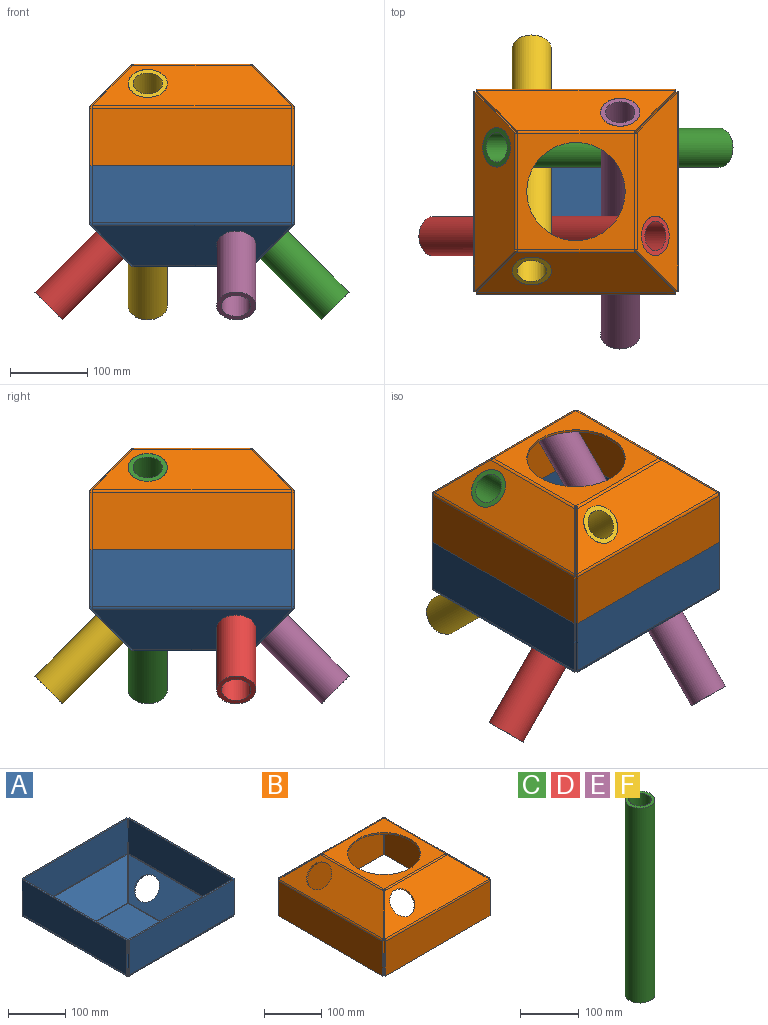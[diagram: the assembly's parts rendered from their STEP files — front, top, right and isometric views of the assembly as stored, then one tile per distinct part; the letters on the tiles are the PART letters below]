
ASSEMBLY  parts=6 mates=5
PART A: 82 faces, bbox 264.7x264.7x131 mm
  f0: plane 150.51x150.51mm, normal (0,0,-1), area 22652.1mm2, adj f20,f40,f60,f80
  f1: plane 150.51x150.51mm, normal (0,0,1), area 22652.1mm2, adj f21,f41,f61,f81
  f2: plane 2.25x2.25mm, normal (0,-0.71,-0.71), area 5.1mm2, adj f3,f7,f8,f18
  f3: plane 53.86x53.86mm, normal (0.82,-0.41,-0.41), area 283.8mm2, adj f2,f7,f8,f15
  f4: plane 2.25x2.25mm, normal (0,-0.71,-0.71), area 5.1mm2, adj f6,f7,f8,f19
  f5: cylinder r=25.4mm len=50.8mm, axis (0,0.71,-0.71), area 506.7mm2, adj f7,f8
  f6: plane 53.86x53.86mm, normal (-0.82,-0.41,-0.41), area 283.8mm2, adj f4,f7,f8,f14
  f7: plane 256.92x51.61mm, normal (0,0.71,-0.71), area 12959mm2, adj f2,f3,f4,f5,f6,f16,f20
  f8: plane 256.92x51.61mm, normal (0,-0.71,0.71), area 12959mm2, adj f2,f3,f4,f5,f6,f17,f21
  f9: plane 258.25x3.18mm, normal (0,0,1), area 820mm2, adj f10,f11,f12,f13
  f10: plane 73.94x3.18mm, normal (1,0,0), area 234.8mm2, adj f9,f12,f13,f15
  f11: plane 73.94x3.18mm, normal (-1,0,0), area 234.8mm2, adj f9,f12,f13,f14
  f12: plane 258.25x73.94mm, normal (0,1,0), area 19094.7mm2, adj f9,f10,f11,f16
  f13: plane 258.25x73.94mm, normal (0,-1,0), area 19094.7mm2, adj f9,f10,f11,f17
  f14: bspline ~3.86x3.84mm, area 10mm2, adj f6,f11,f16,f17
  f15: bspline ~3.86x3.84mm, area 10mm2, adj f3,f10,f16,f17
  f16: cylinder r=5.46mm len=258.25mm, axis (-1,0,0), area 1104.8mm2, adj f7,f12,f14,f15
  f17: cylinder r=2.29mm len=258.25mm, axis (-1,0,0), area 462.5mm2, adj f8,f13,f14,f15
  f18: plane 3.86x3.84mm, normal (1,0,0), area 9.7mm2, adj f2,f20,f21,f79
  f19: plane 3.86x3.84mm, normal (-1,0,0), area 9.7mm2, adj f4,f20,f21,f59
  f20: cylinder r=5.46mm len=150.51mm, axis (1,0,0), area 645.5mm2, adj f0,f7,f18,f19
  f21: cylinder r=2.29mm len=150.51mm, axis (1,0,0), area 270.2mm2, adj f1,f8,f18,f19
  f22: plane 2.25x2.25mm, normal (0,0.71,-0.71), area 5.1mm2, adj f23,f27,f28,f39
  f23: plane 53.86x53.86mm, normal (-0.82,0.41,-0.41), area 283.8mm2, adj f22,f27,f28,f35
  f24: plane 2.25x2.25mm, normal (0,0.71,-0.71), area 5.1mm2, adj f26,f27,f28,f38
  f25: cylinder r=25.4mm len=50.8mm, axis (0,-0.71,-0.71), area 506.7mm2, adj f27,f28
  f26: plane 53.86x53.86mm, normal (0.82,0.41,-0.41), area 283.8mm2, adj f24,f27,f28,f34
  f27: plane 256.92x51.61mm, normal (0,-0.71,-0.71), area 12959mm2, adj f22,f23,f24,f25,f26,f36,f40
  f28: plane 256.92x51.61mm, normal (0,0.71,0.71), area 12959mm2, adj f22,f23,f24,f25,f26,f37,f41
  f29: plane 258.25x3.18mm, normal (0,0,1), area 820mm2, adj f30,f31,f32,f33
  f30: plane 73.94x3.18mm, normal (-1,0,0), area 234.8mm2, adj f29,f32,f33,f35
  f31: plane 73.94x3.18mm, normal (1,0,0), area 234.8mm2, adj f29,f32,f33,f34
  f32: plane 258.25x73.94mm, normal (0,-1,0), area 19094.7mm2, adj f29,f30,f31,f36
  f33: plane 258.25x73.94mm, normal (0,1,0), area 19094.7mm2, adj f29,f30,f31,f37
  f34: bspline ~3.86x3.84mm, area 10mm2, adj f26,f31,f36,f37
  f35: bspline ~3.86x3.84mm, area 10mm2, adj f23,f30,f36,f37
  f36: cylinder r=5.46mm len=258.25mm, axis (1,0,0), area 1104.8mm2, adj f27,f32,f34,f35
  f37: cylinder r=2.29mm len=258.25mm, axis (1,0,0), area 462.5mm2, adj f28,f33,f34,f35
  f38: plane 3.86x3.84mm, normal (1,0,0), area 9.7mm2, adj f24,f40,f41,f78
  f39: plane 3.86x3.84mm, normal (-1,0,0), area 9.7mm2, adj f22,f40,f41,f58
  f40: cylinder r=5.46mm len=150.51mm, axis (1,0,0), area 645.5mm2, adj f0,f27,f38,f39
  f41: cylinder r=2.29mm len=150.51mm, axis (1,0,0), area 270.2mm2, adj f1,f28,f38,f39
  f42: plane 2.25x2.25mm, normal (0.71,0,-0.71), area 5.1mm2, adj f43,f47,f48,f59
  f43: plane 53.86x53.86mm, normal (0.41,0.82,-0.41), area 283.8mm2, adj f42,f47,f48,f55
  f44: plane 2.25x2.25mm, normal (0.71,0,-0.71), area 5.1mm2, adj f46,f47,f48,f58
  f45: cylinder r=25.4mm len=50.8mm, axis (-0.71,0,-0.71), area 506.7mm2, adj f47,f48
  f46: plane 53.86x53.86mm, normal (0.41,-0.82,-0.41), area 283.8mm2, adj f44,f47,f48,f54
  f47: plane 256.92x51.61mm, normal (-0.71,0,-0.71), area 12959mm2, adj f42,f43,f44,f45,f46,f56,f60
  f48: plane 256.92x51.61mm, normal (0.71,0,0.71), area 12959mm2, adj f42,f43,f44,f45,f46,f57,f61
  f49: plane 258.25x3.18mm, normal (0,0,1), area 820mm2, adj f50,f51,f52,f53
  f50: plane 73.94x3.18mm, normal (0,1,0), area 234.8mm2, adj f49,f52,f53,f55
  f51: plane 73.94x3.18mm, normal (0,-1,0), area 234.8mm2, adj f49,f52,f53,f54
  f52: plane 258.25x73.94mm, normal (-1,0,0), area 19094.7mm2, adj f49,f50,f51,f56
  f53: plane 258.25x73.94mm, normal (1,0,0), area 19094.7mm2, adj f49,f50,f51,f57
  f54: bspline ~3.86x3.84mm, area 10mm2, adj f46,f51,f56,f57
  f55: bspline ~3.86x3.84mm, area 10mm2, adj f43,f50,f56,f57
  f56: cylinder r=5.46mm len=258.25mm, axis (0,-1,0), area 1104.8mm2, adj f47,f52,f54,f55
  f57: cylinder r=2.29mm len=258.25mm, axis (0,-1,0), area 462.5mm2, adj f48,f53,f54,f55
  f58: plane 3.86x3.84mm, normal (0,-1,0), area 9.7mm2, adj f39,f44,f60,f61
  f59: plane 3.86x3.84mm, normal (0,1,0), area 9.7mm2, adj f19,f42,f60,f61
  f60: cylinder r=5.46mm len=150.51mm, axis (0,-1,0), area 645.5mm2, adj f0,f47,f58,f59
  f61: cylinder r=2.29mm len=150.51mm, axis (0,-1,0), area 270.2mm2, adj f1,f48,f58,f59
  f62: plane 2.25x2.25mm, normal (-0.71,0,-0.71), area 5.1mm2, adj f63,f67,f68,f78
  f63: plane 53.86x53.86mm, normal (-0.41,-0.82,-0.41), area 283.8mm2, adj f62,f67,f68,f75
  f64: plane 2.25x2.25mm, normal (-0.71,0,-0.71), area 5.1mm2, adj f66,f67,f68,f79
  f65: cylinder r=25.4mm len=50.8mm, axis (0.71,0,-0.71), area 506.7mm2, adj f67,f68
  f66: plane 53.86x53.86mm, normal (-0.41,0.82,-0.41), area 283.8mm2, adj f64,f67,f68,f74
  f67: plane 256.92x51.61mm, normal (0.71,0,-0.71), area 12959mm2, adj f62,f63,f64,f65,f66,f76,f80
  f68: plane 256.92x51.61mm, normal (-0.71,0,0.71), area 12959mm2, adj f62,f63,f64,f65,f66,f77,f81
  f69: plane 258.25x3.18mm, normal (0,0,1), area 820mm2, adj f70,f71,f72,f73
  f70: plane 73.94x3.18mm, normal (0,-1,0), area 234.8mm2, adj f69,f72,f73,f75
  f71: plane 73.94x3.18mm, normal (0,1,0), area 234.8mm2, adj f69,f72,f73,f74
  f72: plane 258.25x73.94mm, normal (1,0,0), area 19094.7mm2, adj f69,f70,f71,f76
  f73: plane 258.25x73.94mm, normal (-1,0,0), area 19094.7mm2, adj f69,f70,f71,f77
  f74: bspline ~3.86x3.84mm, area 10mm2, adj f66,f71,f76,f77
  f75: bspline ~3.86x3.84mm, area 10mm2, adj f63,f70,f76,f77
  f76: cylinder r=5.46mm len=258.25mm, axis (0,1,0), area 1104.8mm2, adj f67,f72,f74,f75
  f77: cylinder r=2.29mm len=258.25mm, axis (0,1,0), area 462.5mm2, adj f68,f73,f74,f75
  f78: plane 3.86x3.84mm, normal (0,-1,0), area 9.7mm2, adj f38,f62,f80,f81
  f79: plane 3.86x3.84mm, normal (0,1,0), area 9.7mm2, adj f18,f64,f80,f81
  f80: cylinder r=5.46mm len=150.51mm, axis (0,-1,0), area 645.5mm2, adj f0,f67,f78,f79
  f81: cylinder r=2.29mm len=150.51mm, axis (0,-1,0), area 270.2mm2, adj f1,f68,f78,f79
PART B: 83 faces, bbox 264.7x264.7x131 mm
  f0: cylinder r=63.5mm len=127mm, axis (0,0,1), area 1266.8mm2, adj f1,f2
  f1: plane 150.51x150.51mm, normal (0,0,-1), area 9984.4mm2, adj f0,f22,f42,f62,f82
  f2: plane 150.51x150.51mm, normal (0,0,1), area 9984.4mm2, adj f0,f21,f41,f61,f81
  f3: plane 2.25x2.25mm, normal (0,0.71,0.71), area 5.1mm2, adj f7,f8,f9,f19
  f4: plane 53.86x53.86mm, normal (-0.82,0.41,0.41), area 283.8mm2, adj f5,f8,f9,f15
  f5: plane 2.25x2.25mm, normal (0,0.71,0.71), area 5.1mm2, adj f4,f8,f9,f20
  f6: cylinder r=25.4mm len=50.8mm, axis (0,0.71,-0.71), area 506.7mm2, adj f8,f9
  f7: plane 53.86x53.86mm, normal (0.82,0.41,0.41), area 283.8mm2, adj f3,f8,f9,f16
  f8: plane 256.92x51.61mm, normal (0,0.71,-0.71), area 12959mm2, adj f3,f4,f5,f6,f7,f18,f22
  f9: plane 256.92x51.61mm, normal (0,-0.71,0.71), area 12959mm2, adj f3,f4,f5,f6,f7,f17,f21
  f10: plane 258.25x3.18mm, normal (0,0,-1), area 820mm2, adj f11,f12,f13,f14
  f11: plane 73.94x3.18mm, normal (-1,0,0), area 234.8mm2, adj f10,f13,f14,f15
  f12: plane 73.94x3.18mm, normal (1,0,0), area 234.8mm2, adj f10,f13,f14,f16
  f13: plane 258.25x73.94mm, normal (0,1,0), area 19094.7mm2, adj f10,f11,f12,f18
  f14: plane 258.25x73.94mm, normal (0,-1,0), area 19094.7mm2, adj f10,f11,f12,f17
  f15: bspline ~3.86x3.84mm, area 10mm2, adj f4,f11,f17,f18
  f16: bspline ~3.86x3.84mm, area 10mm2, adj f7,f12,f17,f18
  f17: cylinder r=5.46mm len=258.25mm, axis (-1,0,0), area 1104.8mm2, adj f9,f14,f15,f16
  f18: cylinder r=2.29mm len=258.25mm, axis (-1,0,0), area 462.5mm2, adj f8,f13,f15,f16
  f19: plane 3.86x3.84mm, normal (1,0,0), area 9.7mm2, adj f3,f21,f22,f80
  f20: plane 3.86x3.84mm, normal (-1,0,0), area 9.7mm2, adj f5,f21,f22,f59
  f21: cylinder r=5.46mm len=150.51mm, axis (1,0,0), area 645.5mm2, adj f2,f9,f19,f20
  f22: cylinder r=2.29mm len=150.51mm, axis (1,0,0), area 270.2mm2, adj f1,f8,f19,f20
  f23: plane 2.25x2.25mm, normal (0,-0.71,0.71), area 5.1mm2, adj f27,f28,f29,f39
  f24: plane 53.86x53.86mm, normal (0.82,-0.41,0.41), area 283.8mm2, adj f25,f28,f29,f35
  f25: plane 2.25x2.25mm, normal (0,-0.71,0.71), area 5.1mm2, adj f24,f28,f29,f40
  f26: cylinder r=25.4mm len=50.8mm, axis (0,-0.71,-0.71), area 506.7mm2, adj f28,f29
  f27: plane 53.86x53.86mm, normal (-0.82,-0.41,0.41), area 283.8mm2, adj f23,f28,f29,f36
  f28: plane 256.92x51.61mm, normal (0,-0.71,-0.71), area 12959mm2, adj f23,f24,f25,f26,f27,f38,f42
  f29: plane 256.92x51.61mm, normal (0,0.71,0.71), area 12959mm2, adj f23,f24,f25,f26,f27,f37,f41
  f30: plane 258.25x3.18mm, normal (0,0,-1), area 820mm2, adj f31,f32,f33,f34
  f31: plane 73.94x3.18mm, normal (1,0,0), area 234.8mm2, adj f30,f33,f34,f35
  f32: plane 73.94x3.18mm, normal (-1,0,0), area 234.8mm2, adj f30,f33,f34,f36
  f33: plane 258.25x73.94mm, normal (0,-1,0), area 19094.7mm2, adj f30,f31,f32,f38
  f34: plane 258.25x73.94mm, normal (0,1,0), area 19094.7mm2, adj f30,f31,f32,f37
  f35: bspline ~3.86x3.84mm, area 10mm2, adj f24,f31,f37,f38
  f36: bspline ~3.86x3.84mm, area 10mm2, adj f27,f32,f37,f38
  f37: cylinder r=5.46mm len=258.25mm, axis (1,0,0), area 1104.8mm2, adj f29,f34,f35,f36
  f38: cylinder r=2.29mm len=258.25mm, axis (1,0,0), area 462.5mm2, adj f28,f33,f35,f36
  f39: plane 3.86x3.84mm, normal (-1,0,0), area 9.7mm2, adj f23,f41,f42,f60
  f40: plane 3.86x3.84mm, normal (1,0,0), area 9.7mm2, adj f25,f41,f42,f79
  f41: cylinder r=5.46mm len=150.51mm, axis (-1,0,0), area 645.5mm2, adj f2,f29,f39,f40
  f42: cylinder r=2.29mm len=150.51mm, axis (-1,0,0), area 270.2mm2, adj f1,f28,f39,f40
  f43: plane 2.25x2.25mm, normal (0.71,0,0.71), area 5.1mm2, adj f47,f48,f49,f59
  f44: plane 53.86x53.86mm, normal (0.41,0.82,0.41), area 283.8mm2, adj f45,f48,f49,f55
  f45: plane 2.25x2.25mm, normal (0.71,0,0.71), area 5.1mm2, adj f44,f48,f49,f60
  f46: cylinder r=25.4mm len=50.8mm, axis (0.71,0,-0.71), area 506.7mm2, adj f48,f49
  f47: plane 53.86x53.86mm, normal (0.41,-0.82,0.41), area 283.8mm2, adj f43,f48,f49,f56
  f48: plane 256.92x51.61mm, normal (0.71,0,-0.71), area 12959mm2, adj f43,f44,f45,f46,f47,f58,f62
  f49: plane 256.92x51.61mm, normal (-0.71,0,0.71), area 12959mm2, adj f43,f44,f45,f46,f47,f57,f61
  f50: plane 258.25x3.18mm, normal (0,0,-1), area 820mm2, adj f51,f52,f53,f54
  f51: plane 73.94x3.18mm, normal (0,1,0), area 234.8mm2, adj f50,f53,f54,f55
  f52: plane 73.94x3.18mm, normal (0,-1,0), area 234.8mm2, adj f50,f53,f54,f56
  f53: plane 258.25x73.94mm, normal (1,0,0), area 19094.7mm2, adj f50,f51,f52,f58
  f54: plane 258.25x73.94mm, normal (-1,0,0), area 19094.7mm2, adj f50,f51,f52,f57
  f55: bspline ~3.86x3.84mm, area 10mm2, adj f44,f51,f57,f58
  f56: bspline ~3.86x3.84mm, area 10mm2, adj f47,f52,f57,f58
  f57: cylinder r=5.46mm len=258.25mm, axis (0,1,0), area 1104.8mm2, adj f49,f54,f55,f56
  f58: cylinder r=2.29mm len=258.25mm, axis (0,1,0), area 462.5mm2, adj f48,f53,f55,f56
  f59: plane 3.86x3.84mm, normal (0,-1,0), area 9.7mm2, adj f20,f43,f61,f62
  f60: plane 3.86x3.84mm, normal (0,1,0), area 9.7mm2, adj f39,f45,f61,f62
  f61: cylinder r=5.46mm len=150.51mm, axis (0,-1,0), area 645.5mm2, adj f2,f49,f59,f60
  f62: cylinder r=2.29mm len=150.51mm, axis (0,-1,0), area 270.2mm2, adj f1,f48,f59,f60
  f63: plane 2.25x2.25mm, normal (-0.71,0,0.71), area 5.1mm2, adj f67,f68,f69,f79
  f64: plane 53.86x53.86mm, normal (-0.41,-0.82,0.41), area 283.8mm2, adj f65,f68,f69,f75
  f65: plane 2.25x2.25mm, normal (-0.71,0,0.71), area 5.1mm2, adj f64,f68,f69,f80
  f66: cylinder r=25.4mm len=50.8mm, axis (-0.71,0,-0.71), area 506.7mm2, adj f68,f69
  f67: plane 53.86x53.86mm, normal (-0.41,0.82,0.41), area 283.8mm2, adj f63,f68,f69,f76
  f68: plane 256.92x51.61mm, normal (-0.71,0,-0.71), area 12959mm2, adj f63,f64,f65,f66,f67,f78,f82
  f69: plane 256.92x51.61mm, normal (0.71,0,0.71), area 12959mm2, adj f63,f64,f65,f66,f67,f77,f81
  f70: plane 258.25x3.18mm, normal (0,0,-1), area 820mm2, adj f71,f72,f73,f74
  f71: plane 73.94x3.18mm, normal (0,-1,0), area 234.8mm2, adj f70,f73,f74,f75
  f72: plane 73.94x3.18mm, normal (0,1,0), area 234.8mm2, adj f70,f73,f74,f76
  f73: plane 258.25x73.94mm, normal (-1,0,0), area 19094.7mm2, adj f70,f71,f72,f78
  f74: plane 258.25x73.94mm, normal (1,0,0), area 19094.7mm2, adj f70,f71,f72,f77
  f75: bspline ~3.86x3.84mm, area 10mm2, adj f64,f71,f77,f78
  f76: bspline ~3.86x3.84mm, area 10mm2, adj f67,f72,f77,f78
  f77: cylinder r=5.46mm len=258.25mm, axis (0,-1,0), area 1104.8mm2, adj f69,f74,f75,f76
  f78: cylinder r=2.29mm len=258.25mm, axis (0,-1,0), area 462.5mm2, adj f68,f73,f75,f76
  f79: plane 3.86x3.84mm, normal (0,1,0), area 9.7mm2, adj f40,f63,f81,f82
  f80: plane 3.86x3.84mm, normal (0,-1,0), area 9.7mm2, adj f19,f65,f81,f82
  f81: cylinder r=5.46mm len=150.51mm, axis (0,1,0), area 645.5mm2, adj f2,f69,f79,f80
  f82: cylinder r=2.29mm len=150.51mm, axis (0,1,0), area 270.2mm2, adj f1,f68,f79,f80
PART C: 4 faces, bbox 50.8x50.8x406.4 mm
  f0: cylinder r=19.05mm len=406.4mm, axis (0,0,-1), area 48643.9mm2, adj f2,f3
  f1: cylinder r=25.4mm len=406.4mm, axis (0,0,-1), area 64858.6mm2, adj f2,f3
  f2: plane 50.8x50.8mm, normal (0,0,1), area 886.7mm2, adj f0,f1
  f3: plane 50.8x50.8mm, normal (0,0,-1), area 886.7mm2, adj f0,f1
PART D: same geometry as C
PART E: same geometry as C
PART F: same geometry as C
PLACE A t=(-87.81,-59.91,36.86)mm
PLACE B t=(-390.01,-33.48,295.71)mm
PLACE C rot(axis=(0,-1,0),45deg) t=(388.34,-28.41,359.27)mm
PLACE D rot(axis=(0,1,0),45deg) t=(18.54,-142.71,-386.15)mm
PLACE E rot(axis=(-1,0,0),45deg) t=(414.97,-254.03,26.21)mm
PLACE F rot(axis=(1,0,0),45deg) t=(300.67,115.76,-53.09)mm
MATE fastened D.f0 <-> B.f66  axis (0.71,0,0.71) through (-66.8,-86.64,273.93)mm
MATE fastened C.f0 <-> B.f46  axis (-0.71,0,0.71) through (-271.74,27.66,273.93)mm
MATE fastened F.f0 <-> B.f6  axis (0,0.71,-0.71) through (-226.42,-131.96,273.93)mm
MATE fastened E.f0 <-> B.f26  axis (0,-0.71,-0.71) through (-112.12,72.99,273.93)mm
MATE fastened B.f10 <-> A.f29  axis (0,0,-1) through (-169.27,-161.81,167.87)mm
